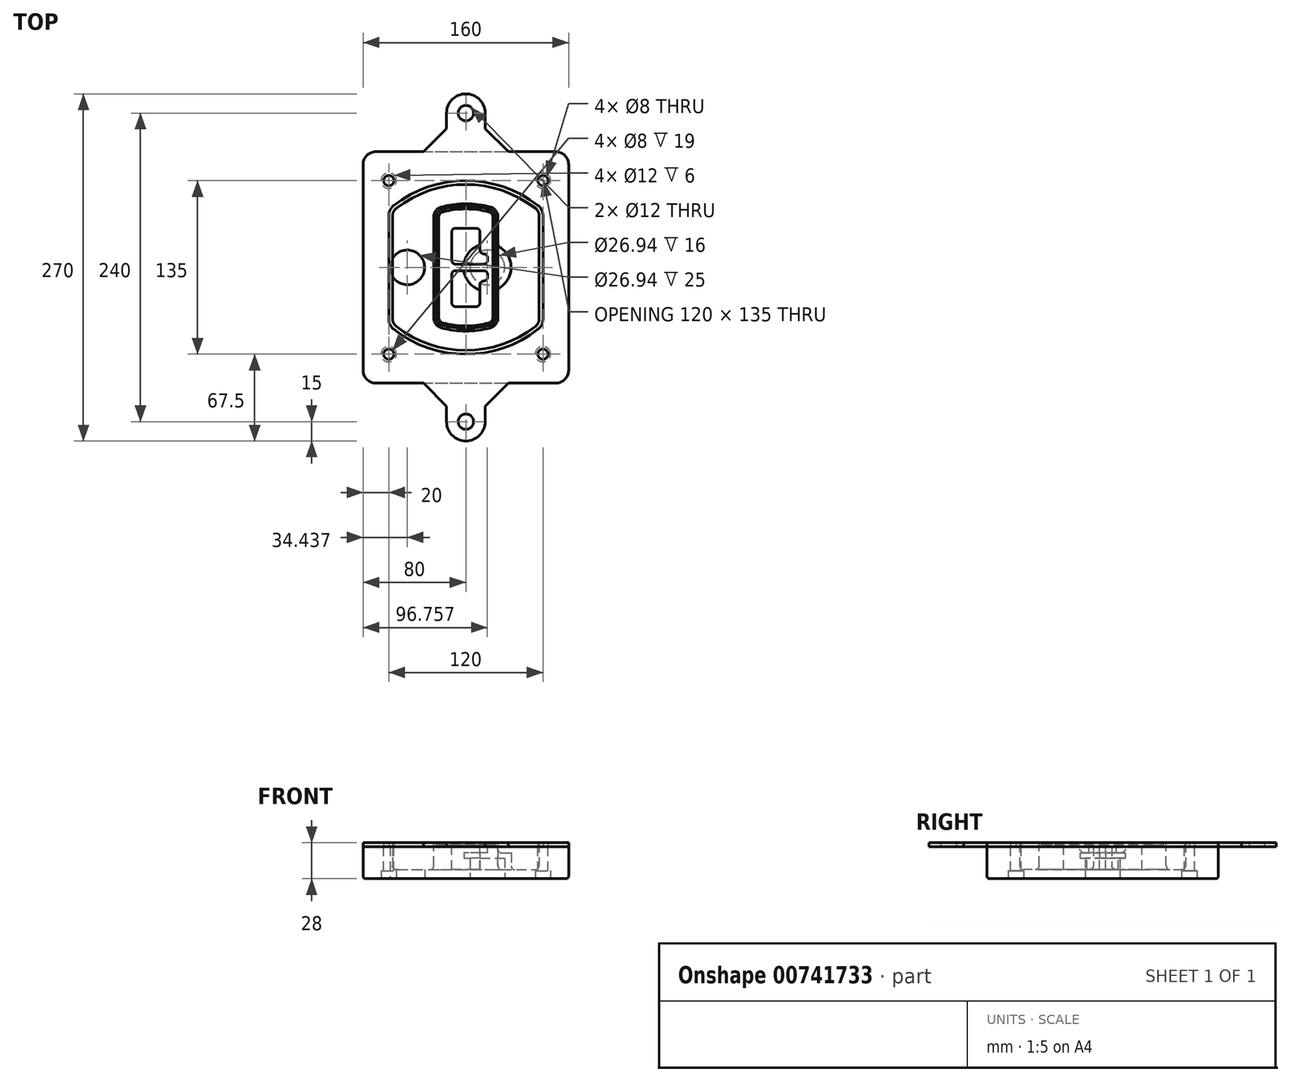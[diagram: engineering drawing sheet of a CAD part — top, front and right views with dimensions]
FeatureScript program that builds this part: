
annotation { "Feature Type Name" : "Feature", "Feature Type Description" : "" }
export const myFeature = defineFeature(function(context is Context, id is Id, definition is map)
    precondition{}
    {
        {
            var Q0;
            Q0=qCreatedBy(makeId("Top.planeOp"),FACE);
            var sketch = newSketch(context, id + "F0", { "sketchPlane" : qUnion([Q0])});
            skPoint(sketch, "E0.rect.middle", {"position": v(0, 0) * mm});
            skLineSegment(sketch, "E1.bottom", {"start": v(-70, -90) * mm, "end": v(70, -90) * mm});
            skLineSegment(sketch, "E1.top", {"start": v(-70, 90) * mm, "end": v(70, 90) * mm});
            skLineSegment(sketch, "E1.left", {"start": v(-80, -80) * mm, "end": v(-80, 80) * mm});
            skLineSegment(sketch, "E1.right", {"start": v(80, -80) * mm, "end": v(80, 80) * mm});
            skLineSegment(sketch, "E2", {"start": v(-80, 90) * mm, "end": v(80, -90) * mm, "construction": true});
            skLineSegment(sketch, "E3", {"start": v(80, 90) * mm, "end": v(-80, -90) * mm, "construction": true});
            skCircle(sketch, "E4", {"center": v(-60, 67.5) * mm, "radius": 4 * mm});
            skCircle(sketch, "E5", {"center": v(60, 67.5) * mm, "radius": 4 * mm});
            skCircle(sketch, "E6", {"center": v(60, -67.5) * mm, "radius": 4 * mm});
            skCircle(sketch, "E7", {"center": v(-60, -67.5) * mm, "radius": 4 * mm});
            skLineSegment(sketch, "E8", {"start": v(-60, 67.5) * mm, "end": v(60, 67.5) * mm, "construction": true});
            skLineSegment(sketch, "E9", {"start": v(60, 67.5) * mm, "end": v(60, -67.5) * mm, "construction": true});
            skLineSegment(sketch, "E10", {"start": v(60, -67.5) * mm, "end": v(-60, -67.5) * mm, "construction": true});
            skLineSegment(sketch, "E11", {"start": v(-60, -67.5) * mm, "end": v(-60, 67.5) * mm, "construction": true});
            skLineSegment(sketch, "E12", {"start": v(-60, 40.3) * mm, "end": v(-60, -40.3) * mm});
            skLineSegment(sketch, "E13", {"start": v(60, 40.3) * mm, "end": v(60, -40.3) * mm});
            skArc(sketch, "E14", {"start": v(56.15, 48.18) * mm, "mid": v(0, 67.5) * mm, "end": v(-56.15, 48.18) * mm});
            skArc(sketch, "E15", {"start": v(-56.15, -48.18) * mm, "mid": v(0, -67.5) * mm, "end": v(56.15, -48.18) * mm});
            skLineSegment(sketch, "E16", {"start": v(-60, 0) * mm, "end": v(60, 0) * mm, "construction": true});
            skPoint(sketch, "E17.visualSharp", {"position": v(-60, -45) * mm});
            skArc(sketch, "E17.filletArc", {"start": v(-60, -40.3) * mm, "mid": v(-58.99, -44.68) * mm, "end": v(-56.15, -48.18) * mm});
            skPoint(sketch, "E18.visualSharp", {"position": v(-60, 45) * mm});
            skArc(sketch, "E18.filletArc", {"start": v(-56.15, 48.18) * mm, "mid": v(-58.99, 44.68) * mm, "end": v(-60, 40.3) * mm});
            skPoint(sketch, "E19.visualSharp", {"position": v(60, 45) * mm});
            skArc(sketch, "E19.filletArc", {"start": v(60, 40.3) * mm, "mid": v(58.99, 44.68) * mm, "end": v(56.15, 48.18) * mm});
            skPoint(sketch, "E20.visualSharp", {"position": v(60, -45) * mm});
            skArc(sketch, "E20.filletArc", {"start": v(56.15, -48.18) * mm, "mid": v(58.99, -44.68) * mm, "end": v(60, -40.3) * mm});
            skPoint(sketch, "E21.visualSharp", {"position": v(-80, 90) * mm});
            skArc(sketch, "E21.filletArc", {"start": v(-70, 90) * mm, "mid": v(-77.07, 87.07) * mm, "end": v(-80, 80) * mm});
            skPoint(sketch, "E22.visualSharp", {"position": v(80, 90) * mm});
            skArc(sketch, "E22.filletArc", {"start": v(80, 80) * mm, "mid": v(77.07, 87.07) * mm, "end": v(70, 90) * mm});
            skPoint(sketch, "E23.visualSharp", {"position": v(80, -90) * mm});
            skArc(sketch, "E23.filletArc", {"start": v(70, -90) * mm, "mid": v(77.07, -87.07) * mm, "end": v(80, -80) * mm});
            skPoint(sketch, "E24.visualSharp", {"position": v(-80, -90) * mm});
            skArc(sketch, "E24.filletArc", {"start": v(-80, -80) * mm, "mid": v(-77.07, -87.07) * mm, "end": v(-70, -90) * mm});
            skArc(sketch, "E25.0", {"start": v(57, 40.3) * mm, "mid": v(56.3, 43.36) * mm, "end": v(54.3, 45.81) * mm});
            skLineSegment(sketch, "E25.1", {"start": v(57, 40.3) * mm, "end": v(57, -40.3) * mm});
            skArc(sketch, "E25.2", {"start": v(54.3, -45.81) * mm, "mid": v(56.3, -43.36) * mm, "end": v(57, -40.3) * mm});
            skArc(sketch, "E25.3", {"start": v(-54.3, -45.81) * mm, "mid": v(0, -64.5) * mm, "end": v(54.3, -45.81) * mm});
            skArc(sketch, "E25.4", {"start": v(-57, -40.3) * mm, "mid": v(-56.3, -43.36) * mm, "end": v(-54.3, -45.81) * mm});
            skArc(sketch, "E25.5", {"start": v(54.3, 45.81) * mm, "mid": v(0, 64.5) * mm, "end": v(-54.3, 45.81) * mm});
            skLineSegment(sketch, "E25.6", {"start": v(-57, 40.3) * mm, "end": v(-57, -40.3) * mm});
            skArc(sketch, "E25.7", {"start": v(-54.3, 45.81) * mm, "mid": v(-56.3, 43.36) * mm, "end": v(-57, 40.3) * mm});
            skArc(sketch, "E26.0", {"start": v(-58.62, 51.33) * mm, "mid": v(-62.58, 46.43) * mm, "end": v(-64, 40.3) * mm});
            skArc(sketch, "E26.1", {"start": v(58.62, 51.33) * mm, "mid": v(0, 71.5) * mm, "end": v(-58.62, 51.33) * mm});
            skArc(sketch, "E26.2", {"start": v(64, 40.3) * mm, "mid": v(62.58, 46.43) * mm, "end": v(58.62, 51.33) * mm});
            skLineSegment(sketch, "E26.3", {"start": v(64, 40.3) * mm, "end": v(64, -40.3) * mm});
            skArc(sketch, "E26.4", {"start": v(58.62, -51.33) * mm, "mid": v(62.58, -46.43) * mm, "end": v(64, -40.3) * mm});
            skLineSegment(sketch, "E26.5", {"start": v(-64, 40.3) * mm, "end": v(-64, -40.3) * mm});
            skArc(sketch, "E26.6", {"start": v(-58.62, -51.33) * mm, "mid": v(0, -71.5) * mm, "end": v(58.62, -51.33) * mm});
            skArc(sketch, "E26.7", {"start": v(-64, -40.3) * mm, "mid": v(-62.58, -46.43) * mm, "end": v(-58.62, -51.33) * mm});
            skSolve(sketch);
        }
        {
            var Q0;
            Q0=makeQuery(id+"F0.imprint","IMPRINT",FACE,{"disambiguationData":[TD([[makeQuery(id+"F0.imprint","IMPRINT",EDGE,{"derivedFrom":sQuery(id+"F0.wireOp",EDGE,"E1.bottom")}),1.0]])]});
            var Q1;
            Q1=makeQuery(id+"F0.imprint","IMPRINT",FACE,{"disambiguationData":[TD([[makeQuery(id+"F0.imprint","IMPRINT",EDGE,{"derivedFrom":sQuery(id+"F0.wireOp",EDGE,"E12")}),1.0]])]});
            var Q2;
            Q2=makeQuery(id+"F0.imprint","IMPRINT",FACE,{"disambiguationData":[TD([[makeQuery(id+"F0.imprint","IMPRINT",EDGE,{"derivedFrom":sQuery(id+"F0.wireOp",EDGE,"E25.0")}),1.0]])]});
            var Q3;
            Q3=makeQuery(id+"F0.imprint","IMPRINT",FACE,{"disambiguationData":[TD([[makeQuery(id+"F0.imprint","IMPRINT",EDGE,{"derivedFrom":sQuery(id+"F0.wireOp",EDGE,"E12")}),-1.0]])]});
            extrude(context, id + "F1", {"entities" : qUnion([Q0, Q1, Q2, Q3]), "oppositeDirection" : true, "depth" : 25 * mm});
        }
        {
            var Q0;
            Q0=makeQuery(id+"F0.imprint","IMPRINT",FACE,{"disambiguationData":[TD([[makeQuery(id+"F0.imprint","IMPRINT",EDGE,{"derivedFrom":sQuery(id+"F0.wireOp",EDGE,"E12")}),1.0]])]});
            extrude(context, id + "F2", {"entities" : qUnion([Q0]), "operationType" : NewBodyOperationType.ADD, "depth" : 3 * mm});
        }
        {
            var Q0;
            Q0=makeQuery(id+"F0.imprint","IMPRINT",FACE,{"disambiguationData":[TD([[makeQuery(id+"F0.imprint","IMPRINT",EDGE,{"derivedFrom":sQuery(id+"F0.wireOp",EDGE,"E25.0")}),1.0]])]});
            extrude(context, id + "F3", {"entities" : qUnion([Q0]), "operationType" : NewBodyOperationType.REMOVE, "oppositeDirection" : true, "depth" : 18 * mm});
        }
        {
            var Q0;
            Q0=makeQuery(id+"F2.opExtrude","CAP_FACE",FACE,{"disambiguationData":[OSD([sQuery(id+"F0.wireOp",EDGE,"E12"),sQuery(id+"F0.wireOp",EDGE,"E13"),sQuery(id+"F0.wireOp",EDGE,"E14"),sQuery(id+"F0.wireOp",EDGE,"E15"),sQuery(id+"F0.wireOp",EDGE,"E17.filletArc"),sQuery(id+"F0.wireOp",EDGE,"E18.filletArc"),sQuery(id+"F0.wireOp",EDGE,"E19.filletArc"),sQuery(id+"F0.wireOp",EDGE,"E20.filletArc"),sQuery(id+"F0.wireOp",EDGE,"E25.0"),sQuery(id+"F0.wireOp",EDGE,"E25.1"),sQuery(id+"F0.wireOp",EDGE,"E25.2"),sQuery(id+"F0.wireOp",EDGE,"E25.3"),sQuery(id+"F0.wireOp",EDGE,"E25.4"),sQuery(id+"F0.wireOp",EDGE,"E25.5"),sQuery(id+"F0.wireOp",EDGE,"E25.6"),sQuery(id+"F0.wireOp",EDGE,"E25.7")])],"isStart":false});
            var sketch = newSketch(context, id + "F4", { "sketchPlane" : qUnion([Q0])});
            skArc(sketch, "E27.0", {"start": v(-19.08, -46.97) * mm, "mid": v(0, -49.5) * mm, "end": v(19.08, -46.97) * mm});
            skArc(sketch, "E28.0", {"start": v(19.08, 46.97) * mm, "mid": v(0, 49.5) * mm, "end": v(-19.08, 46.97) * mm});
            skLineSegment(sketch, "E29", {"start": v(-25, 39.25) * mm, "end": v(-25, -39.25) * mm});
            skLineSegment(sketch, "E30", {"start": v(25, 39.25) * mm, "end": v(25, -39.25) * mm});
            skLineSegment(sketch, "E31", {"start": v(-25, 45.1) * mm, "end": v(25, 45.1) * mm, "construction": true});
            skLineSegment(sketch, "E32", {"start": v(-25, -45.1) * mm, "end": v(25, -45.1) * mm, "construction": true});
            skPoint(sketch, "E33.visualSharp", {"position": v(-25, 45.1) * mm});
            skArc(sketch, "E33.filletArc", {"start": v(-19.08, 46.97) * mm, "mid": v(-23.35, 44.11) * mm, "end": v(-25, 39.25) * mm});
            skPoint(sketch, "E34.visualSharp", {"position": v(25, 45.1) * mm});
            skArc(sketch, "E34.filletArc", {"start": v(25, 39.25) * mm, "mid": v(23.35, 44.11) * mm, "end": v(19.08, 46.97) * mm});
            skPoint(sketch, "E35.visualSharp", {"position": v(25, -45.1) * mm});
            skArc(sketch, "E35.filletArc", {"start": v(19.08, -46.97) * mm, "mid": v(23.35, -44.11) * mm, "end": v(25, -39.25) * mm});
            skPoint(sketch, "E36.visualSharp", {"position": v(-25, -45.1) * mm});
            skArc(sketch, "E36.filletArc", {"start": v(-25, -39.25) * mm, "mid": v(-23.35, -44.11) * mm, "end": v(-19.08, -46.97) * mm});
            skArc(sketch, "E37.0", {"start": v(54.3, 45.81) * mm, "mid": v(0, 64.5) * mm, "end": v(-54.3, 45.81) * mm});
            skArc(sketch, "E37.1", {"start": v(-54.3, 45.81) * mm, "mid": v(-56.3, 43.36) * mm, "end": v(-57, 40.3) * mm});
            skLineSegment(sketch, "E37.2", {"start": v(-57, 40.3) * mm, "end": v(-57, -40.3) * mm});
            skArc(sketch, "E37.3", {"start": v(-57, -40.3) * mm, "mid": v(-56.3, -43.36) * mm, "end": v(-54.3, -45.81) * mm});
            skArc(sketch, "E37.4", {"start": v(-54.3, -45.81) * mm, "mid": v(0, -64.5) * mm, "end": v(54.3, -45.81) * mm});
            skArc(sketch, "E37.5", {"start": v(54.3, -45.81) * mm, "mid": v(56.3, -43.36) * mm, "end": v(57, -40.3) * mm});
            skLineSegment(sketch, "E37.6", {"start": v(57, 40.3) * mm, "end": v(57, -40.3) * mm});
            skArc(sketch, "E37.7", {"start": v(57, 40.3) * mm, "mid": v(56.3, 43.36) * mm, "end": v(54.3, 45.81) * mm});
            skLineSegment(sketch, "E38.0", {"start": v(23, 39.25) * mm, "end": v(23, -39.25) * mm});
            skArc(sketch, "E38.1", {"start": v(18.56, -45.04) * mm, "mid": v(21.76, -42.9) * mm, "end": v(23, -39.25) * mm});
            skArc(sketch, "E38.2", {"start": v(-18.56, -45.04) * mm, "mid": v(0, -47.5) * mm, "end": v(18.56, -45.04) * mm});
            skArc(sketch, "E38.3", {"start": v(-23, -39.25) * mm, "mid": v(-21.76, -42.9) * mm, "end": v(-18.56, -45.04) * mm});
            skLineSegment(sketch, "E38.4", {"start": v(-23, 39.25) * mm, "end": v(-23, -39.25) * mm});
            skArc(sketch, "E38.5", {"start": v(23, 39.25) * mm, "mid": v(21.76, 42.9) * mm, "end": v(18.56, 45.04) * mm});
            skArc(sketch, "E38.6", {"start": v(-18.56, 45.04) * mm, "mid": v(-21.76, 42.9) * mm, "end": v(-23, 39.25) * mm});
            skArc(sketch, "E38.7", {"start": v(18.56, 45.04) * mm, "mid": v(0, 47.5) * mm, "end": v(-18.56, 45.04) * mm});
            skArc(sketch, "E39.0", {"start": v(21, 39.25) * mm, "mid": v(20.18, 41.68) * mm, "end": v(18.04, 43.1) * mm});
            skLineSegment(sketch, "E39.1", {"start": v(21, 39.25) * mm, "end": v(21, -39.25) * mm});
            skArc(sketch, "E39.2", {"start": v(18.04, -43.1) * mm, "mid": v(20.18, -41.68) * mm, "end": v(21, -39.25) * mm});
            skArc(sketch, "E39.3", {"start": v(-18.04, -43.1) * mm, "mid": v(0, -45.5) * mm, "end": v(18.04, -43.1) * mm});
            skArc(sketch, "E39.4", {"start": v(-21, -39.25) * mm, "mid": v(-20.18, -41.68) * mm, "end": v(-18.04, -43.1) * mm});
            skArc(sketch, "E39.5", {"start": v(18.04, 43.1) * mm, "mid": v(0, 45.5) * mm, "end": v(-18.04, 43.1) * mm});
            skLineSegment(sketch, "E39.6", {"start": v(-21, 39.25) * mm, "end": v(-21, -39.25) * mm});
            skArc(sketch, "E39.7", {"start": v(-18.04, 43.1) * mm, "mid": v(-20.18, 41.68) * mm, "end": v(-21, 39.25) * mm});
            skLineSegment(sketch, "E40", {"start": v(-25, 0) * mm, "end": v(25, 0) * mm, "construction": true});
            skLineSegment(sketch, "E41", {"start": v(-11, 5.5) * mm, "end": v(-11, 27.5) * mm});
            skLineSegment(sketch, "E42", {"start": v(-8, 30.5) * mm, "end": v(8, 30.5) * mm});
            skLineSegment(sketch, "E43", {"start": v(11, 27.5) * mm, "end": v(11, 13.5) * mm});
            skLineSegment(sketch, "E44", {"start": v(14, 10.5) * mm, "end": v(14, 10.5) * mm});
            skLineSegment(sketch, "E45", {"start": v(17, 7.5) * mm, "end": v(17, 5.5) * mm});
            skLineSegment(sketch, "E46", {"start": v(14, 2.5) * mm, "end": v(-8, 2.5) * mm});
            skPoint(sketch, "E47.visualSharp", {"position": v(-11, 30.5) * mm});
            skArc(sketch, "E47.filletArc", {"start": v(-8, 30.5) * mm, "mid": v(-10.12, 29.62) * mm, "end": v(-11, 27.5) * mm});
            skPoint(sketch, "E48.visualSharp", {"position": v(11, 30.5) * mm});
            skArc(sketch, "E48.filletArc", {"start": v(11, 27.5) * mm, "mid": v(10.12, 29.62) * mm, "end": v(8, 30.5) * mm});
            skPoint(sketch, "E49.visualSharp", {"position": v(11, 10.5) * mm});
            skArc(sketch, "E49.filletArc", {"start": v(11, 13.5) * mm, "mid": v(11.88, 11.38) * mm, "end": v(14, 10.5) * mm});
            skPoint(sketch, "E50.visualSharp", {"position": v(17, 10.5) * mm});
            skArc(sketch, "E50.filletArc", {"start": v(17, 7.5) * mm, "mid": v(16.12, 9.62) * mm, "end": v(14, 10.5) * mm});
            skPoint(sketch, "E51.visualSharp", {"position": v(17, 2.5) * mm});
            skArc(sketch, "E51.filletArc", {"start": v(14, 2.5) * mm, "mid": v(16.12, 3.38) * mm, "end": v(17, 5.5) * mm});
            skPoint(sketch, "E52.visualSharp", {"position": v(-11, 2.5) * mm});
            skArc(sketch, "E52.filletArc", {"start": v(-11, 5.5) * mm, "mid": v(-10.12, 3.38) * mm, "end": v(-8, 2.5) * mm});
            skLineSegment(sketch, "E53.0.MirrorCS", {"start": v(14, -2.5) * mm, "end": v(-8, -2.5) * mm});
            skArc(sketch, "E54.0.MirrorCS", {"start": v(-11, -5.5) * mm, "mid": v(-10.12, -3.38) * mm, "end": v(-8, -2.5) * mm});
            skLineSegment(sketch, "E55.0.MirrorCS", {"start": v(-11, -5.5) * mm, "end": v(-11, -27.5) * mm});
            skArc(sketch, "E56.0.MirrorCS", {"start": v(-8, -30.5) * mm, "mid": v(-10.12, -29.62) * mm, "end": v(-11, -27.5) * mm});
            skLineSegment(sketch, "E57.0.MirrorCS", {"start": v(-8, -30.5) * mm, "end": v(8, -30.5) * mm});
            skArc(sketch, "E58.0.MirrorCS", {"start": v(11, -27.5) * mm, "mid": v(10.12, -29.62) * mm, "end": v(8, -30.5) * mm});
            skLineSegment(sketch, "E59.0.MirrorCS", {"start": v(11, -27.5) * mm, "end": v(11, -13.5) * mm});
            skArc(sketch, "E60.0.MirrorCS", {"start": v(11, -13.5) * mm, "mid": v(11.88, -11.38) * mm, "end": v(14, -10.5) * mm});
            skArc(sketch, "E61.0.MirrorCS", {"start": v(17, -7.5) * mm, "mid": v(16.12, -9.62) * mm, "end": v(14, -10.5) * mm});
            skLineSegment(sketch, "E62.0.MirrorCS", {"start": v(17, -7.5) * mm, "end": v(17, -5.5) * mm});
            skArc(sketch, "E63.0.MirrorCS", {"start": v(14, -2.5) * mm, "mid": v(16.12, -3.38) * mm, "end": v(17, -5.5) * mm});
            skSolve(sketch);
        }
        {
            var Q0;
            Q0=makeQuery(id+"F4.imprint","IMPRINT",FACE,{"disambiguationData":[TD([[makeQuery(id+"F4.imprint","IMPRINT",EDGE,{"derivedFrom":sQuery(id+"F4.wireOp",EDGE,"E27.0")}),1.0]])]});
            var Q1;
            Q1=makeQuery(id+"F4.imprint","IMPRINT",FACE,{"disambiguationData":[TD([[makeQuery(id+"F4.imprint","IMPRINT",EDGE,{"derivedFrom":sQuery(id+"F4.wireOp",EDGE,"E38.0")}),-1.0]])]});
            var Q2;
            Q2=makeQuery(id+"F4.imprint","IMPRINT",FACE,{"disambiguationData":[TD([[makeQuery(id+"F4.imprint","IMPRINT",EDGE,{"derivedFrom":sQuery(id+"F4.wireOp",EDGE,"E39.0")}),1.0]])]});
            extrude(context, id + "F5", {"entities" : qUnion([Q0, Q1, Q2]), "operationType" : NewBodyOperationType.ADD, "endBound" : BoundingType.UP_TO_NEXT, "oppositeDirection" : true, "depth" : 25 * mm});
        }
        {
            var Q0;
            Q0=makeQuery(id+"F4.imprint","IMPRINT",FACE,{"disambiguationData":[TD([[makeQuery(id+"F4.imprint","IMPRINT",EDGE,{"derivedFrom":sQuery(id+"F4.wireOp",EDGE,"E38.0")}),-1.0]])]});
            extrude(context, id + "F6", {"entities" : qUnion([Q0]), "operationType" : NewBodyOperationType.REMOVE, "oppositeDirection" : true, "depth" : 2 * mm});
        }
        {
            var Q0;
            Q0=makeQuery(id+"F1.opExtrude","CAP_FACE",FACE,{"disambiguationData":[OSD([sQuery(id+"F0.wireOp",EDGE,"E1.bottom"),sQuery(id+"F0.wireOp",EDGE,"E1.top"),sQuery(id+"F0.wireOp",EDGE,"E1.left"),sQuery(id+"F0.wireOp",EDGE,"E1.right"),sQuery(id+"F0.wireOp",EDGE,"E4"),sQuery(id+"F0.wireOp",EDGE,"E5"),sQuery(id+"F0.wireOp",EDGE,"E6"),sQuery(id+"F0.wireOp",EDGE,"E7"),sQuery(id+"F0.wireOp",EDGE,"E21.filletArc"),sQuery(id+"F0.wireOp",EDGE,"E22.filletArc"),sQuery(id+"F0.wireOp",EDGE,"E23.filletArc"),sQuery(id+"F0.wireOp",EDGE,"E24.filletArc")])],"isStart":false});
            var sketch = newSketch(context, id + "F7", { "sketchPlane" : qUnion([Q0])});
            skCircle(sketch, "E64", {"center": v(16.76, 0) * mm, "radius": 13.47 * mm});
            skCircle(sketch, "E65", {"center": v(-45.56, 0) * mm, "radius": 13.47 * mm});
            skLineSegment(sketch, "E66", {"start": v(80, 0) * mm, "end": v(-80, 0) * mm});
            skCircle(sketch, "E67", {"center": v(16.76, 0) * mm, "radius": 18.47 * mm});
            skCircle(sketch, "E68", {"center": v(60, -67.5) * mm, "radius": 6 * mm});
            skCircle(sketch, "E69", {"center": v(-60, -67.5) * mm, "radius": 6 * mm});
            skCircle(sketch, "E70", {"center": v(-60, 67.5) * mm, "radius": 6 * mm});
            skCircle(sketch, "E71", {"center": v(60, 67.5) * mm, "radius": 6 * mm});
            skSolve(sketch);
        }
        {
            var Q0;
            {var subQ1=sQuery(id+"F7.wireOp",EDGE,"E66");var subQ4=sQuery(id+"F7.wireOp",EDGE,"E64");var subQ6=makeQuery(id+"F7.imprint","INTERSECT",VERTEX,{"disambiguationData":[OD(0.0)],"derivedFrom":[subQ4,subQ1]});Q0=makeQuery(id+"F7.imprint","IMPRINT",FACE,{"disambiguationData":[TD([[makeQuery(id+"F7.imprint","IMPRINT",EDGE,{"disambiguationData":[TD([[subQ6,-1.0]])],"derivedFrom":subQ4}),-1.0]])]});}
            var Q1;
            {var subQ0=sQuery(id+"F7.wireOp",EDGE,"E66");var subQ1=sQuery(id+"F7.wireOp",EDGE,"E64");var subQ3=makeQuery(id+"F7.imprint","INTERSECT",VERTEX,{"disambiguationData":[OD(0.0)],"derivedFrom":[subQ1,subQ0]});Q1=makeQuery(id+"F7.imprint","IMPRINT",FACE,{"disambiguationData":[TD([[makeQuery(id+"F7.imprint","IMPRINT",EDGE,{"disambiguationData":[TD([[subQ3,-1.0]])],"derivedFrom":subQ1}),1.0]])]});}
            var Q2;
            {var subQ0=sQuery(id+"F7.wireOp",EDGE,"E66");var subQ1=sQuery(id+"F7.wireOp",EDGE,"E64");var subQ3=makeQuery(id+"F7.imprint","INTERSECT",VERTEX,{"disambiguationData":[OD(0.0)],"derivedFrom":[subQ1,subQ0]});Q2=makeQuery(id+"F7.imprint","IMPRINT",FACE,{"disambiguationData":[TD([[makeQuery(id+"F7.imprint","IMPRINT",EDGE,{"disambiguationData":[TD([[subQ3,1.0]])],"derivedFrom":subQ1}),1.0]])]});}
            var Q3;
            {var subQ1=sQuery(id+"F7.wireOp",EDGE,"E66");var subQ4=sQuery(id+"F7.wireOp",EDGE,"E64");var subQ6=makeQuery(id+"F7.imprint","INTERSECT",VERTEX,{"disambiguationData":[OD(0.0)],"derivedFrom":[subQ4,subQ1]});Q3=makeQuery(id+"F7.imprint","IMPRINT",FACE,{"disambiguationData":[TD([[makeQuery(id+"F7.imprint","IMPRINT",EDGE,{"disambiguationData":[TD([[subQ6,1.0]])],"derivedFrom":subQ4}),-1.0]])]});}
            extrude(context, id + "F8", {"entities" : qUnion([Q0, Q1, Q2, Q3]), "operationType" : NewBodyOperationType.ADD, "oppositeDirection" : true, "depth" : 20 * mm});
        }
        {
            var Q0;
            {var subQ0=sQuery(id+"F7.wireOp",EDGE,"E66");var subQ1=sQuery(id+"F7.wireOp",EDGE,"E64");var subQ3=makeQuery(id+"F7.imprint","INTERSECT",VERTEX,{"disambiguationData":[OD(0.0)],"derivedFrom":[subQ1,subQ0]});Q0=makeQuery(id+"F7.imprint","IMPRINT",FACE,{"disambiguationData":[TD([[makeQuery(id+"F7.imprint","IMPRINT",EDGE,{"disambiguationData":[TD([[subQ3,-1.0]])],"derivedFrom":subQ1}),1.0]])]});}
            var Q1;
            {var subQ0=sQuery(id+"F7.wireOp",EDGE,"E66");var subQ1=sQuery(id+"F7.wireOp",EDGE,"E64");var subQ3=makeQuery(id+"F7.imprint","INTERSECT",VERTEX,{"disambiguationData":[OD(0.0)],"derivedFrom":[subQ1,subQ0]});Q1=makeQuery(id+"F7.imprint","IMPRINT",FACE,{"disambiguationData":[TD([[makeQuery(id+"F7.imprint","IMPRINT",EDGE,{"disambiguationData":[TD([[subQ3,1.0]])],"derivedFrom":subQ1}),1.0]])]});}
            extrude(context, id + "F9", {"entities" : qUnion([Q0, Q1]), "operationType" : NewBodyOperationType.REMOVE, "oppositeDirection" : true, "depth" : 16 * mm});
        }
        {
            var Q0;
            {var subQ0=sQuery(id+"F7.wireOp",EDGE,"E66");var subQ1=sQuery(id+"F7.wireOp",EDGE,"E65");var subQ3=makeQuery(id+"F7.imprint","INTERSECT",VERTEX,{"disambiguationData":[OD(0.0)],"derivedFrom":[subQ1,subQ0]});Q0=makeQuery(id+"F7.imprint","IMPRINT",FACE,{"disambiguationData":[TD([[makeQuery(id+"F7.imprint","IMPRINT",EDGE,{"disambiguationData":[TD([[subQ3,-1.0]])],"derivedFrom":subQ1}),1.0]])]});}
            var Q1;
            {var subQ0=sQuery(id+"F7.wireOp",EDGE,"E66");var subQ1=sQuery(id+"F7.wireOp",EDGE,"E65");var subQ3=makeQuery(id+"F7.imprint","INTERSECT",VERTEX,{"disambiguationData":[OD(0.0)],"derivedFrom":[subQ1,subQ0]});Q1=makeQuery(id+"F7.imprint","IMPRINT",FACE,{"disambiguationData":[TD([[makeQuery(id+"F7.imprint","IMPRINT",EDGE,{"disambiguationData":[TD([[subQ3,1.0]])],"derivedFrom":subQ1}),1.0]])]});}
            extrude(context, id + "F10", {"entities" : qUnion([Q0, Q1]), "operationType" : NewBodyOperationType.REMOVE, "oppositeDirection" : true, "depth" : 25 * mm});
        }
        {
            var Q0;
            Q0=makeQuery(id+"F7.imprint","IMPRINT",FACE,{"disambiguationData":[TD([[makeQuery(id+"F7.imprint","IMPRINT",EDGE,{"derivedFrom":sQuery(id+"F7.wireOp",EDGE,"E68")}),1.0]])]});
            var Q1;
            Q1=makeQuery(id+"F7.imprint","IMPRINT",FACE,{"disambiguationData":[TD([[makeQuery(id+"F7.imprint","IMPRINT",EDGE,{"derivedFrom":makeQuery(id+"F1.opExtrude","CAP_EDGE",EDGE,{"disambiguationData":[OSD([sQuery(id+"F0.wireOp",EDGE,"E5")])],"isStart":false})}),-1.0]])]});
            var Q2;
            Q2=makeQuery(id+"F7.imprint","IMPRINT",FACE,{"disambiguationData":[TD([[makeQuery(id+"F7.imprint","IMPRINT",EDGE,{"derivedFrom":sQuery(id+"F7.wireOp",EDGE,"E69")}),1.0]])]});
            var Q3;
            Q3=makeQuery(id+"F7.imprint","IMPRINT",FACE,{"disambiguationData":[TD([[makeQuery(id+"F7.imprint","IMPRINT",EDGE,{"derivedFrom":makeQuery(id+"F1.opExtrude","CAP_EDGE",EDGE,{"disambiguationData":[OSD([sQuery(id+"F0.wireOp",EDGE,"E4")])],"isStart":false})}),-1.0]])]});
            var Q4;
            Q4=makeQuery(id+"F7.imprint","IMPRINT",FACE,{"disambiguationData":[TD([[makeQuery(id+"F7.imprint","IMPRINT",EDGE,{"derivedFrom":sQuery(id+"F7.wireOp",EDGE,"E70")}),1.0]])]});
            var Q5;
            Q5=makeQuery(id+"F7.imprint","IMPRINT",FACE,{"disambiguationData":[TD([[makeQuery(id+"F7.imprint","IMPRINT",EDGE,{"derivedFrom":makeQuery(id+"F1.opExtrude","CAP_EDGE",EDGE,{"disambiguationData":[OSD([sQuery(id+"F0.wireOp",EDGE,"E7")])],"isStart":false})}),-1.0]])]});
            var Q6;
            Q6=makeQuery(id+"F7.imprint","IMPRINT",FACE,{"disambiguationData":[TD([[makeQuery(id+"F7.imprint","IMPRINT",EDGE,{"derivedFrom":sQuery(id+"F7.wireOp",EDGE,"E71")}),1.0]])]});
            var Q7;
            Q7=makeQuery(id+"F7.imprint","IMPRINT",FACE,{"disambiguationData":[TD([[makeQuery(id+"F7.imprint","IMPRINT",EDGE,{"derivedFrom":makeQuery(id+"F1.opExtrude","CAP_EDGE",EDGE,{"disambiguationData":[OSD([sQuery(id+"F0.wireOp",EDGE,"E6")])],"isStart":false})}),-1.0]])]});
            extrude(context, id + "F11", {"entities" : qUnion([Q0, Q1, Q2, Q3, Q4, Q5, Q6, Q7]), "operationType" : NewBodyOperationType.REMOVE, "oppositeDirection" : true, "depth" : 6 * mm});
        }
        {
            var Q0;
            Q0=makeQuery(id+"F9.boolean.opBoolean","COPY",FACE,{"derivedFrom":makeQuery(id+"F9.opExtrude","CAP_FACE",FACE,{"disambiguationData":[OSD([sQuery(id+"F7.wireOp",EDGE,"E64")])],"isStart":false})});
            var sketch = newSketch(context, id + "F12", { "sketchPlane" : qUnion([Q0])});
            skArc(sketch, "E72.0", {"start": v(11, 17.55) * mm, "mid": v(2.57, 11.82) * mm, "end": v(-1.54, 2.5) * mm});
            skArc(sketch, "E72.1", {"start": v(-1.54, -2.5) * mm, "mid": v(2.57, -11.82) * mm, "end": v(11, -17.55) * mm});
            skLineSegment(sketch, "E73", {"start": v(-1.54, -2.5) * mm, "end": v(14, -2.5) * mm});
            skLineSegment(sketch, "E74.0", {"start": v(14, 2.5) * mm, "end": v(-1.54, 2.5) * mm});
            skArc(sketch, "E74.1", {"start": v(14, 2.5) * mm, "mid": v(16.12, 3.38) * mm, "end": v(17, 5.5) * mm});
            skLineSegment(sketch, "E74.2", {"start": v(17, 7.5) * mm, "end": v(17, 5.5) * mm});
            skArc(sketch, "E74.3", {"start": v(17, 7.5) * mm, "mid": v(16.12, 9.62) * mm, "end": v(14, 10.5) * mm});
            skArc(sketch, "E74.4", {"start": v(11, 13.5) * mm, "mid": v(11.88, 11.38) * mm, "end": v(14, 10.5) * mm});
            skLineSegment(sketch, "E74.5", {"start": v(11, 17.55) * mm, "end": v(11, 13.5) * mm});
            skLineSegment(sketch, "E74.7", {"start": v(14, -2.5) * mm, "end": v(-1.54, -2.5) * mm});
            skArc(sketch, "E74.8", {"start": v(14, -2.5) * mm, "mid": v(16.12, -3.38) * mm, "end": v(17, -5.5) * mm});
            skLineSegment(sketch, "E74.9", {"start": v(17, -7.5) * mm, "end": v(17, -5.5) * mm});
            skArc(sketch, "E74.10", {"start": v(17, -7.5) * mm, "mid": v(16.12, -9.62) * mm, "end": v(14, -10.5) * mm});
            skArc(sketch, "E74.11", {"start": v(11, -13.5) * mm, "mid": v(11.88, -11.38) * mm, "end": v(14, -10.5) * mm});
            skLineSegment(sketch, "E74.12", {"start": v(11, -17.55) * mm, "end": v(11, -13.5) * mm});
            skPoint(sketch, "E75.orphan", {"position": v(11, -27.5) * mm});
            skPoint(sketch, "E76.orphan", {"position": v(-8, -2.5) * mm});
            skPoint(sketch, "E77.orphan", {"position": v(-8, 2.5) * mm});
            skPoint(sketch, "E78.orphan", {"position": v(11, 27.5) * mm});
            skSolve(sketch);
        }
        {
            var Q0;
            {var subQ7=sQuery(id+"F12.wireOp",EDGE,"E72.0");var subQ14=sQuery(id+"F12.wireOp",EDGE,"E72.1");var subQ16=sQuery(id+"F12.wireOp",EDGE,"E74.1");var subQ18=sQuery(id+"F12.wireOp",EDGE,"E74.8");Q0=qUnion([makeQuery(id+"F12.imprint","IMPRINT",FACE,{"disambiguationData":[TD([[makeQuery(id+"F12.imprint","IMPRINT",EDGE,{"derivedFrom":subQ7}),1.0]])]}),makeQuery(id+"F12.imprint","IMPRINT",FACE,{"disambiguationData":[TD([[makeQuery(id+"F12.imprint","IMPRINT",EDGE,{"derivedFrom":subQ14}),1.0]])]}),makeQuery(id+"F12.imprint","IMPRINT",FACE,{"disambiguationData":[TD([[makeQuery(id+"F12.imprint","IMPRINT",EDGE,{"derivedFrom":subQ16}),1.0]])]}),makeQuery(id+"F12.imprint","IMPRINT",FACE,{"disambiguationData":[TD([[makeQuery(id+"F12.imprint","IMPRINT",EDGE,{"derivedFrom":subQ18}),-1.0]])]})]);}
            var Q1;
            Q1=makeQuery(id+"F5.boolean.opBoolean","SPLIT",FACE,{"disambiguationData":[TD([makeQuery(id+"F5.opExtrude","SWEPT_FACE",FACE,{"disambiguationData":[OSD([sQuery(id+"F4.wireOp",EDGE,"E41")])]})])],"derivedFrom":makeQuery(id+"F3.boolean.opBoolean","COPY",FACE,{"derivedFrom":makeQuery(id+"F3.opExtrude","CAP_FACE",FACE,{"disambiguationData":[OSD([sQuery(id+"F0.wireOp",EDGE,"E25.0"),sQuery(id+"F0.wireOp",EDGE,"E25.1"),sQuery(id+"F0.wireOp",EDGE,"E25.2"),sQuery(id+"F0.wireOp",EDGE,"E25.3"),sQuery(id+"F0.wireOp",EDGE,"E25.4"),sQuery(id+"F0.wireOp",EDGE,"E25.5"),sQuery(id+"F0.wireOp",EDGE,"E25.6"),sQuery(id+"F0.wireOp",EDGE,"E25.7")])],"isStart":false})})});
            extrude(context, id + "F13", {"entities" : qUnion([Q0]), "operationType" : NewBodyOperationType.REMOVE, "endBound" : BoundingType.UP_TO_SURFACE, "endBoundEntityFace" : qUnion([Q1]), "depth" : 25 * mm});
        }
        {
            var Q0;
            Q0=makeQuery(id+"F3.boolean.opBoolean","COPY",EDGE,{"derivedFrom":makeQuery(id+"F3.opExtrude","CAP_EDGE",EDGE,{"disambiguationData":[OSD([sQuery(id+"F0.wireOp",EDGE,"E25.6")])],"isStart":false})});
            var Q1;
            Q1=makeQuery(id+"F8.boolean.opBoolean","INTERSECT",EDGE,{"derivedFrom":[makeQuery(id+"F5.opExtrude","SWEPT_FACE",FACE,{"disambiguationData":[OSD([sQuery(id+"F4.wireOp",EDGE,"E30")])]}),makeQuery(id+"F8.opExtrude","CAP_FACE",FACE,{"disambiguationData":[OSD([sQuery(id+"F7.wireOp",EDGE,"E67")])],"isStart":false})]});
            var Q2;
            Q2=makeQuery(id+"F8.boolean.opBoolean","INTERSECT",EDGE,{"disambiguationData":[OD(1.0)],"derivedFrom":[makeQuery(id+"F5.opExtrude","SWEPT_FACE",FACE,{"disambiguationData":[OSD([sQuery(id+"F4.wireOp",EDGE,"E30")])]}),makeQuery(id+"F8.opExtrude","SWEPT_FACE",FACE,{"disambiguationData":[OSD([sQuery(id+"F7.wireOp",EDGE,"E67")])]})]});
            var Q3;
            {var subQ0=sQuery(id+"F4.wireOp",EDGE,"E30");Q3=makeQuery(id+"F8.boolean.opBoolean","SPLIT",EDGE,{"disambiguationData":[TD([makeQuery(id+"F5.opExtrude","SWEPT_FACE",FACE,{"disambiguationData":[OSD([sQuery(id+"F4.wireOp",EDGE,"E35.filletArc")])]})])],"derivedFrom":makeQuery(id+"F5.opExtrude","CAP_EDGE",EDGE,{"disambiguationData":[OSD([subQ0])],"isStart":false})});}
            var Q4;
            {var subQ0=sQuery(id+"F0.wireOp",EDGE,"E25.7");var subQ1=sQuery(id+"F0.wireOp",EDGE,"E25.1");var subQ2=sQuery(id+"F0.wireOp",EDGE,"E25.6");var subQ3=sQuery(id+"F0.wireOp",EDGE,"E25.5");var subQ4=sQuery(id+"F0.wireOp",EDGE,"E25.4");var subQ5=sQuery(id+"F0.wireOp",EDGE,"E25.0");var subQ6=sQuery(id+"F0.wireOp",EDGE,"E25.2");var subQ7=sQuery(id+"F0.wireOp",EDGE,"E25.3");Q4=makeQuery(id+"F8.boolean.opBoolean","INTERSECT",EDGE,{"derivedFrom":[makeQuery(id+"F5.boolean.opBoolean","SPLIT",FACE,{"disambiguationData":[TD([makeQuery(id+"F2.opExtrude","SWEPT_FACE",FACE,{"disambiguationData":[OSD([subQ5])]})])],"derivedFrom":makeQuery(id+"F3.boolean.opBoolean","COPY",FACE,{"derivedFrom":makeQuery(id+"F3.opExtrude","CAP_FACE",FACE,{"disambiguationData":[OSD([subQ5,subQ1,subQ6,subQ7,subQ4,subQ3,subQ2,subQ0])],"isStart":false})})}),makeQuery(id+"F8.opExtrude","SWEPT_FACE",FACE,{"disambiguationData":[OSD([sQuery(id+"F7.wireOp",EDGE,"E67")])]})]});}
            var Q5;
            Q5=makeQuery(id+"F8.boolean.opBoolean","INTERSECT",EDGE,{"disambiguationData":[OD(0.0)],"derivedFrom":[makeQuery(id+"F5.opExtrude","SWEPT_FACE",FACE,{"disambiguationData":[OSD([sQuery(id+"F4.wireOp",EDGE,"E30")])]}),makeQuery(id+"F8.opExtrude","SWEPT_FACE",FACE,{"disambiguationData":[OSD([sQuery(id+"F7.wireOp",EDGE,"E67")])]})]});
            fillet(context, id + "F14", {"entities" : qUnion([Q0, Q1, Q2, Q3, Q4, Q5]), "radius" : 3 * mm, "tangentPropagation" : true, "allowEdgeOverflow" : false});
        }
        {
            var Q0;
            Q0=makeQuery(id+"F1.opExtrude","CAP_EDGE",EDGE,{"disambiguationData":[OSD([sQuery(id+"F0.wireOp",EDGE,"E1.bottom")])],"isStart":false});
            fillet(context, id + "F15", {"entities" : qUnion([Q0]), "radius" : 2 * mm, "tangentPropagation" : true, "allowEdgeOverflow" : false});
        }
        {
            var Q0;
            {var subQ0=sQuery(id+"F0.wireOp",EDGE,"E21.filletArc");var subQ1=sQuery(id+"F0.wireOp",EDGE,"E7");var subQ2=sQuery(id+"F0.wireOp",EDGE,"E6");var subQ3=sQuery(id+"F0.wireOp",EDGE,"E5");var subQ4=sQuery(id+"F0.wireOp",EDGE,"E4");var subQ5=sQuery(id+"F0.wireOp",EDGE,"E22.filletArc");var subQ6=sQuery(id+"F0.wireOp",EDGE,"E1.bottom");var subQ7=sQuery(id+"F0.wireOp",EDGE,"E1.right");var subQ8=sQuery(id+"F0.wireOp",EDGE,"E1.top");var subQ9=sQuery(id+"F0.wireOp",EDGE,"E1.left");var subQ10=sQuery(id+"F0.wireOp",EDGE,"E23.filletArc");var subQ11=sQuery(id+"F0.wireOp",EDGE,"E24.filletArc");Q0=makeQuery(id+"F2.boolean.opBoolean","SPLIT",FACE,{"disambiguationData":[TD([makeQuery(id+"F1.opExtrude","SWEPT_FACE",FACE,{"disambiguationData":[OSD([subQ6])]})])],"derivedFrom":makeQuery(id+"F1.opExtrude","CAP_FACE",FACE,{"disambiguationData":[OSD([subQ6,subQ8,subQ9,subQ7,subQ4,subQ3,subQ2,subQ1,subQ0,subQ5,subQ10,subQ11])],"isStart":true})});}
            var sketch = newSketch(context, id + "F16", { "sketchPlane" : qUnion([Q0])});
            skLineSegment(sketch, "E79.0", {"start": v(-70, 90) * mm, "end": v(70, 90) * mm});
            skLineSegment(sketch, "E79.1", {"start": v(-70, -90) * mm, "end": v(70, -90) * mm});
            skLineSegment(sketch, "E79.2", {"start": v(80, -80) * mm, "end": v(80, 80) * mm});
            skLineSegment(sketch, "E79.3", {"start": v(-80, -80) * mm, "end": v(-80, 80) * mm});
            skArc(sketch, "E79.4", {"start": v(-70, 90) * mm, "mid": v(-77.07, 87.07) * mm, "end": v(-80, 80) * mm});
            skCircle(sketch, "E79.5", {"center": v(-60, -67.5) * mm, "radius": 4 * mm});
            skCircle(sketch, "E79.6", {"center": v(60, -67.5) * mm, "radius": 4 * mm});
            skArc(sketch, "E79.7", {"start": v(70, -90) * mm, "mid": v(77.07, -87.07) * mm, "end": v(80, -80) * mm});
            skArc(sketch, "E79.8", {"start": v(80, 80) * mm, "mid": v(77.07, 87.07) * mm, "end": v(70, 90) * mm});
            skCircle(sketch, "E79.9", {"center": v(60, 67.5) * mm, "radius": 4 * mm});
            skCircle(sketch, "E79.10", {"center": v(-60, 67.5) * mm, "radius": 4 * mm});
            skLineSegment(sketch, "E79.11", {"start": v(-60, 40.3) * mm, "end": v(-60, -40.3) * mm});
            skArc(sketch, "E79.12", {"start": v(56.15, 48.18) * mm, "mid": v(0, 67.5) * mm, "end": v(-56.15, 48.18) * mm});
            skLineSegment(sketch, "E79.13", {"start": v(60, 40.3) * mm, "end": v(60, -40.3) * mm});
            skArc(sketch, "E79.14", {"start": v(-56.15, -48.18) * mm, "mid": v(0, -67.5) * mm, "end": v(56.15, -48.18) * mm});
            skArc(sketch, "E79.15", {"start": v(-56.15, 48.18) * mm, "mid": v(-58.99, 44.68) * mm, "end": v(-60, 40.3) * mm});
            skArc(sketch, "E79.16", {"start": v(60, 40.3) * mm, "mid": v(58.99, 44.68) * mm, "end": v(56.15, 48.18) * mm});
            skArc(sketch, "E79.17", {"start": v(56.15, -48.18) * mm, "mid": v(58.99, -44.68) * mm, "end": v(60, -40.3) * mm});
            skArc(sketch, "E79.18", {"start": v(-60, -40.3) * mm, "mid": v(-58.99, -44.68) * mm, "end": v(-56.15, -48.18) * mm});
            skPoint(sketch, "E79.19", {"position": v(-58.99, 44.68) * mm});
            skCircle(sketch, "E80", {"center": v(0, 120) * mm, "radius": 6 * mm});
            skPoint(sketch, "E80.centerSnap0", {"position": v(0, 90) * mm});
            skLineSegment(sketch, "E81", {"start": v(0, 23.75) * mm, "end": v(0, 120) * mm, "construction": true});
            skLineSegment(sketch, "E82", {"start": v(15, 120) * mm, "end": v(15, 108) * mm});
            skLineSegment(sketch, "E83", {"start": v(15, 108) * mm, "end": v(33, 90) * mm});
            skLineSegment(sketch, "E84", {"start": v(-15, 120) * mm, "end": v(-15, 108) * mm});
            skArc(sketch, "E85", {"start": v(15, 120) * mm, "mid": v(0, 135) * mm, "end": v(-15, 120) * mm});
            skLineSegment(sketch, "E86", {"start": v(-15, 108) * mm, "end": v(-33, 90) * mm});
            skLineSegment(sketch, "E87", {"start": v(-80, 0) * mm, "end": v(80, 0) * mm, "construction": true});
            skArc(sketch, "E88.MirrorCS", {"start": v(56.15, 48.18) * mm, "mid": v(58.99, 44.68) * mm, "end": v(60, 40.3) * mm});
            skArc(sketch, "E89.MirrorCS", {"start": v(-60, 40.3) * mm, "mid": v(-58.99, 44.68) * mm, "end": v(-56.15, 48.18) * mm});
            skArc(sketch, "E90.MirrorCS", {"start": v(-80, 80) * mm, "mid": v(-77.07, 87.07) * mm, "end": v(-70, 90) * mm});
            skLineSegment(sketch, "E91.MirrorCS", {"start": v(70, 90) * mm, "end": v(-70, 90) * mm});
            skPoint(sketch, "E92.MirrorP", {"position": v(58.99, 44.68) * mm});
            skArc(sketch, "E93.MirrorCS", {"start": v(70, 90) * mm, "mid": v(77.07, 87.07) * mm, "end": v(80, 80) * mm});
            skArc(sketch, "E94.MirrorCS", {"start": v(-56.15, 48.18) * mm, "mid": v(0, 67.5) * mm, "end": v(56.15, 48.18) * mm});
            skArc(sketch, "E95.MirrorCS", {"start": v(-15, 120) * mm, "mid": v(0, 135) * mm, "end": v(15, 120) * mm});
            skArc(sketch, "E96.MirrorCS", {"start": v(60, -40.3) * mm, "mid": v(58.99, -44.68) * mm, "end": v(56.15, -48.18) * mm});
            skArc(sketch, "E97.MirrorCS", {"start": v(-56.15, -48.18) * mm, "mid": v(-58.99, -44.68) * mm, "end": v(-60, -40.3) * mm});
            skArc(sketch, "E98.MirrorCS", {"start": v(80, -80) * mm, "mid": v(77.07, -87.07) * mm, "end": v(70, -90) * mm});
            skPoint(sketch, "E99.MirrorP", {"position": v(0, -90) * mm});
            skLineSegment(sketch, "E100.MirrorCS", {"start": v(15, -120) * mm, "end": v(15, -108) * mm});
            skLineSegment(sketch, "E101.MirrorCS", {"start": v(-15, -120) * mm, "end": v(-15, -108) * mm});
            skArc(sketch, "E102.MirrorCS", {"start": v(-15, -120) * mm, "mid": v(0, -135) * mm, "end": v(15, -120) * mm});
            skLineSegment(sketch, "E103.MirrorCS", {"start": v(-15, -108) * mm, "end": v(-33, -90) * mm});
            skCircle(sketch, "E104.MirrorC", {"center": v(0, -120) * mm, "radius": 6 * mm});
            skArc(sketch, "E105.MirrorCS", {"start": v(-70, -90) * mm, "mid": v(-77.07, -87.07) * mm, "end": v(-80, -80) * mm});
            skLineSegment(sketch, "E106.MirrorCS", {"start": v(15, -108) * mm, "end": v(33, -90) * mm});
            skArc(sketch, "E107.MirrorCS", {"start": v(-80, -80) * mm, "mid": v(-77.07, -87.07) * mm, "end": v(-70, -90) * mm});
            skArc(sketch, "E108.MirrorCS", {"start": v(15, -120) * mm, "mid": v(0, -135) * mm, "end": v(-15, -120) * mm});
            skLineSegment(sketch, "E109.MirrorCS", {"start": v(70, -90) * mm, "end": v(-70, -90) * mm});
            skPoint(sketch, "E110.MirrorP", {"position": v(-58.99, -44.68) * mm});
            skArc(sketch, "E111.MirrorCS", {"start": v(56.15, -48.18) * mm, "mid": v(0, -67.5) * mm, "end": v(-56.15, -48.18) * mm});
            skPoint(sketch, "E112.MirrorP", {"position": v(58.99, -44.68) * mm});
            skLineSegment(sketch, "E113.MirrorCS", {"start": v(0, -23.75) * mm, "end": v(0, -120) * mm, "construction": true});
            skSolve(sketch);
        }
        {
            var Q0;
            Q0=makeQuery(id+"F16.imprint","IMPRINT",FACE,{"disambiguationData":[TD([[makeQuery(id+"F16.imprint","IMPRINT",EDGE,{"derivedFrom":sQuery(id+"F16.wireOp",EDGE,"E104.MirrorC")}),-1.0]])]});
            var Q1;
            Q1=makeQuery(id+"F16.imprint","IMPRINT",FACE,{"disambiguationData":[TD([[makeQuery(id+"F16.imprint","IMPRINT",EDGE,{"derivedFrom":sQuery(id+"F16.wireOp",EDGE,"E79.2")}),1.0]])]});
            var Q2;
            Q2=makeQuery(id+"F16.imprint","IMPRINT",FACE,{"disambiguationData":[TD([[makeQuery(id+"F16.imprint","IMPRINT",EDGE,{"derivedFrom":sQuery(id+"F16.wireOp",EDGE,"E80")}),-1.0]])]});
            var Q3;
            Q3=makeQuery(id+"F2.opExtrude","CAP_FACE",FACE,{"disambiguationData":[OSD([sQuery(id+"F0.wireOp",EDGE,"E12"),sQuery(id+"F0.wireOp",EDGE,"E13"),sQuery(id+"F0.wireOp",EDGE,"E14"),sQuery(id+"F0.wireOp",EDGE,"E15"),sQuery(id+"F0.wireOp",EDGE,"E17.filletArc"),sQuery(id+"F0.wireOp",EDGE,"E18.filletArc"),sQuery(id+"F0.wireOp",EDGE,"E19.filletArc"),sQuery(id+"F0.wireOp",EDGE,"E20.filletArc"),sQuery(id+"F0.wireOp",EDGE,"E25.0"),sQuery(id+"F0.wireOp",EDGE,"E25.1"),sQuery(id+"F0.wireOp",EDGE,"E25.2"),sQuery(id+"F0.wireOp",EDGE,"E25.3"),sQuery(id+"F0.wireOp",EDGE,"E25.4"),sQuery(id+"F0.wireOp",EDGE,"E25.5"),sQuery(id+"F0.wireOp",EDGE,"E25.6"),sQuery(id+"F0.wireOp",EDGE,"E25.7")])],"isStart":false});
            extrude(context, id + "F17", {"entities" : qUnion([Q0, Q1, Q2]), "endBound" : BoundingType.UP_TO_SURFACE, "depth" : 25 * mm, "endBoundEntityFace" : qUnion([Q3]), "offsetDistance" : 25 * mm});
        }
    });
